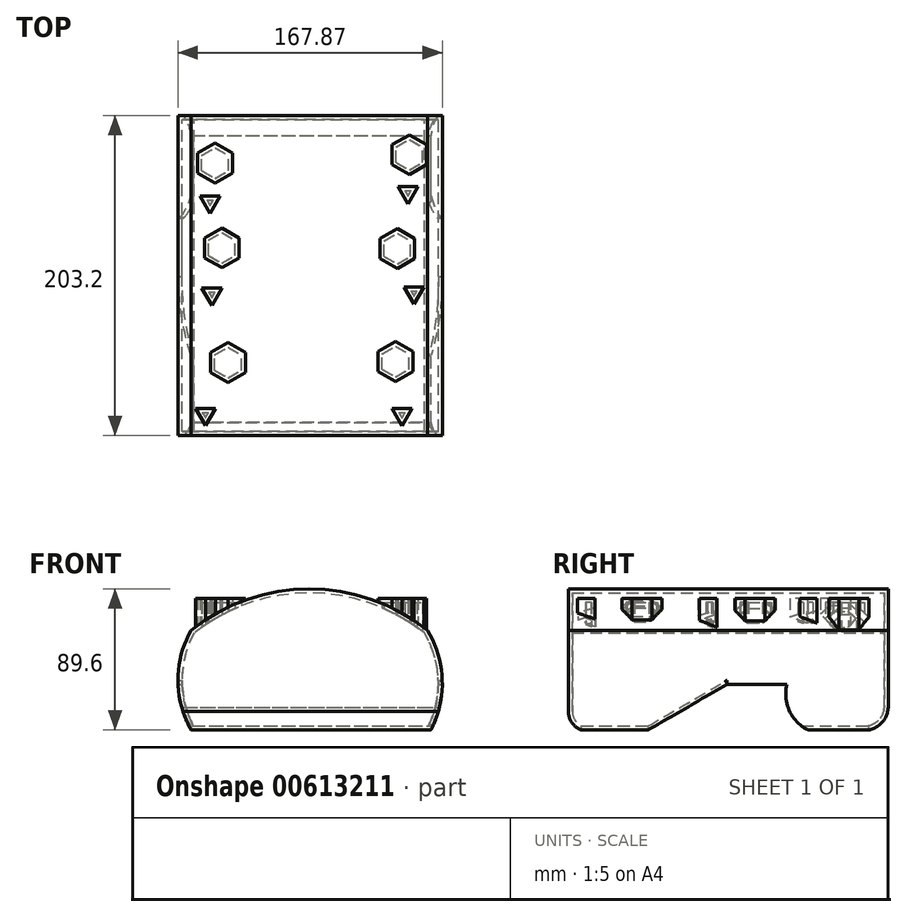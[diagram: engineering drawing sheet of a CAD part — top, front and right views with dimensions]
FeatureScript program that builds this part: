
annotation { "Feature Type Name" : "Feature", "Feature Type Description" : "" }
export const myFeature = defineFeature(function(context is Context, id is Id, definition is map)
    precondition{}
    {
        {
            var Q0;
            Q0=qCreatedBy(makeId("Front.planeOp"),FACE);
            var sketch = newSketch(context, id + "F0", { "sketchPlane" : qUnion([Q0])});
            skLineSegment(sketch, "E0", {"start": v(-76.06, 0) * mm, "end": v(76.35, 0) * mm});
            skArc(sketch, "E1", {"start": v(-76.06, 63.32) * mm, "mid": v(-84.33, 31.66) * mm, "end": v(-76.06, 0) * mm});
            skArc(sketch, "E2", {"start": v(76.35, 0) * mm, "mid": v(83.5, 31.95) * mm, "end": v(74.11, 63.32) * mm});
            skArc(sketch, "E3", {"start": v(74.11, 63.32) * mm, "mid": v(-0.97, 89.6) * mm, "end": v(-76.06, 63.32) * mm});
            skSolve(sketch);
        }
        {
            var Q0;
            Q0 = qSketchRegion(id + "F0", true);
            extrude(context, id + "F1", {"entities" : qUnion([Q0]), "depth" : 203.2 * mm, "offsetDistance" : 25.4 * mm});
        }
        {
            var Q0;
            Q0=qCreatedBy(makeId("Right.planeOp"),FACE);
            var sketch = newSketch(context, id + "F2", { "sketchPlane" : qUnion([Q0])});
            skLineSegment(sketch, "E4", {"start": v(-152.44, 0) * mm, "end": v(-102.37, 29.07) * mm});
            skArc(sketch, "E5", {"start": v(-64.27, 29.07) * mm, "mid": v(-62.7, 12.14) * mm, "end": v(-50.8, 0) * mm});
            skLineSegment(sketch, "E6", {"start": v(-102.37, 29.07) * mm, "end": v(-64.27, 29.07) * mm});
            skLineSegment(sketch, "E7", {"start": v(-152.44, 0) * mm, "end": v(-50.8, 0) * mm});
            skLineSegment(sketch, "E8.0", {"start": v(-203.2, 0) * mm, "end": v(-203.2, 63.32) * mm});
            skLineSegment(sketch, "E9.0", {"start": v(-203.2, 0) * mm, "end": v(0, 0) * mm});
            skArc(sketch, "E10", {"start": v(-203.2, 11.78) * mm, "mid": v(-200.91, 4.68) * mm, "end": v(-195.1, 0) * mm});
            skLineSegment(sketch, "E11", {"start": v(-203.2, 11.78) * mm, "end": v(-203.2, 0) * mm});
            skLineSegment(sketch, "E12", {"start": v(-195.1, 0) * mm, "end": v(-203.2, 0) * mm});
            skArc(sketch, "E13", {"start": v(-12.65, 0) * mm, "mid": v(-3.78, 4.94) * mm, "end": v(0, 14.37) * mm});
            skLineSegment(sketch, "E14", {"start": v(-12.65, 0) * mm, "end": v(0, 0) * mm});
            skLineSegment(sketch, "E15", {"start": v(0, 14.37) * mm, "end": v(0, 0) * mm});
            skSolve(sketch);
        }
        {
            var Q0;
            Q0 = qSketchRegion(id + "F2", true);
            var Q1;
            Q1=sQuery(id+"F2.wireOp",EDGE,"E4");
            var Q2;
            Q2=sQuery(id+"F2.wireOp",EDGE,"wQtt1t4y-miuZ-OvXZ-mnIg-CTxD3PF6We9W");
            var Q3;
            Q3=sQuery(id+"F2.wireOp",EDGE,"E5");
            extrude(context, id + "F3", {"entities" : qUnion([Q0]), "operationType" : NewBodyOperationType.REMOVE, "surfaceEntities" : qUnion([Q1, Q2, Q3]), "oppositeDirection" : true, "depth" : 203.2 * mm, "offsetDistance" : 25.4 * mm, "symmetric" : true});
        }
        {
            var Q0;
            Q0=makeQuery(id+"F3.boolean.opBoolean","COPY",FACE,{"derivedFrom":makeQuery(id+"F3.opExtrude","SWEPT_FACE",FACE,{"disambiguationData":[OSD([sQuery(id+"F2.wireOp",EDGE,"E6")])]})});
            var sketch = newSketch(context, id + "F4", { "sketchPlane" : qUnion([Q0])});
            skLineSegment(sketch, "E16", {"start": v(-67.5, 90.4) * mm, "end": v(-56.47, 96.7) * mm});
            skLineSegment(sketch, "E17", {"start": v(-56.47, 96.7) * mm, "end": v(-45.44, 90.4) * mm});
            skLineSegment(sketch, "E18", {"start": v(-45.44, 90.4) * mm, "end": v(-45.44, 77.7) * mm});
            skLineSegment(sketch, "E19", {"start": v(-67.5, 90.4) * mm, "end": v(-67.5, 77.7) * mm});
            skLineSegment(sketch, "E20", {"start": v(-67.5, 77.7) * mm, "end": v(-56.47, 71.4) * mm});
            skLineSegment(sketch, "E21", {"start": v(-56.47, 71.4) * mm, "end": v(-45.44, 77.7) * mm});
            skLineSegment(sketch, "E22", {"start": v(-63.65, 163.33) * mm, "end": v(-52.62, 169.63) * mm});
            skLineSegment(sketch, "E23", {"start": v(-52.62, 169.63) * mm, "end": v(-41.6, 163.33) * mm});
            skLineSegment(sketch, "E24", {"start": v(-41.6, 163.33) * mm, "end": v(-41.6, 150.63) * mm});
            skLineSegment(sketch, "E25", {"start": v(-63.65, 163.33) * mm, "end": v(-63.65, 150.63) * mm});
            skLineSegment(sketch, "E26", {"start": v(-63.65, 150.63) * mm, "end": v(-52.62, 144.34) * mm});
            skLineSegment(sketch, "E27", {"start": v(-52.62, 144.34) * mm, "end": v(-41.6, 150.63) * mm});
            skLineSegment(sketch, "E28", {"start": v(-71.84, 36.59) * mm, "end": v(-60.8, 42.89) * mm});
            skLineSegment(sketch, "E29", {"start": v(-60.8, 42.89) * mm, "end": v(-49.78, 36.59) * mm});
            skLineSegment(sketch, "E30", {"start": v(-49.78, 36.59) * mm, "end": v(-49.78, 23.89) * mm});
            skLineSegment(sketch, "E31", {"start": v(-71.84, 36.59) * mm, "end": v(-71.84, 23.89) * mm});
            skLineSegment(sketch, "E32", {"start": v(-71.84, 23.89) * mm, "end": v(-60.8, 17.59) * mm});
            skLineSegment(sketch, "E33", {"start": v(-60.8, 17.59) * mm, "end": v(-49.78, 23.89) * mm});
            skLineSegment(sketch, "E34", {"start": v(51.56, 31.3) * mm, "end": v(62.6, 37.6) * mm});
            skLineSegment(sketch, "E35", {"start": v(62.6, 37.6) * mm, "end": v(73.62, 31.3) * mm});
            skLineSegment(sketch, "E36", {"start": v(73.62, 31.3) * mm, "end": v(73.62, 18.6) * mm});
            skLineSegment(sketch, "E37", {"start": v(51.56, 31.3) * mm, "end": v(51.56, 18.6) * mm});
            skLineSegment(sketch, "E38", {"start": v(51.56, 18.6) * mm, "end": v(62.6, 12.3) * mm});
            skLineSegment(sketch, "E39", {"start": v(62.6, 12.3) * mm, "end": v(73.62, 18.6) * mm});
            skLineSegment(sketch, "E40", {"start": v(42.78, 162.7) * mm, "end": v(53.8, 169) * mm});
            skLineSegment(sketch, "E41", {"start": v(53.8, 169) * mm, "end": v(64.83, 162.7) * mm});
            skLineSegment(sketch, "E42", {"start": v(64.83, 162.7) * mm, "end": v(64.83, 150) * mm});
            skLineSegment(sketch, "E43", {"start": v(42.78, 162.7) * mm, "end": v(42.78, 150) * mm});
            skLineSegment(sketch, "E44", {"start": v(42.78, 150) * mm, "end": v(53.8, 143.7) * mm});
            skLineSegment(sketch, "E45", {"start": v(53.8, 143.7) * mm, "end": v(64.83, 150) * mm});
            skLineSegment(sketch, "E46", {"start": v(43.95, 90.94) * mm, "end": v(54.98, 97.24) * mm});
            skLineSegment(sketch, "E47", {"start": v(54.98, 97.24) * mm, "end": v(66, 90.94) * mm});
            skLineSegment(sketch, "E48", {"start": v(66, 90.94) * mm, "end": v(66, 78.24) * mm});
            skLineSegment(sketch, "E49", {"start": v(43.95, 90.94) * mm, "end": v(43.95, 78.24) * mm});
            skLineSegment(sketch, "E50", {"start": v(43.95, 78.24) * mm, "end": v(54.98, 71.94) * mm});
            skLineSegment(sketch, "E51", {"start": v(54.98, 71.94) * mm, "end": v(66, 78.24) * mm});
            skLineSegment(sketch, "E52", {"start": v(51.56, 186.24) * mm, "end": v(64.26, 186.24) * mm});
            skLineSegment(sketch, "E53", {"start": v(51.56, 186.24) * mm, "end": v(57.91, 197.24) * mm});
            skLineSegment(sketch, "E54", {"start": v(57.91, 197.24) * mm, "end": v(64.26, 186.24) * mm});
            skLineSegment(sketch, "E55", {"start": v(-73.3, 185.97) * mm, "end": v(-60.6, 185.97) * mm});
            skLineSegment(sketch, "E56", {"start": v(-73.3, 185.97) * mm, "end": v(-66.96, 196.97) * mm});
            skLineSegment(sketch, "E57", {"start": v(-66.96, 196.97) * mm, "end": v(-60.6, 185.97) * mm});
            skLineSegment(sketch, "E58", {"start": v(59.15, 108.8) * mm, "end": v(71.85, 108.8) * mm});
            skLineSegment(sketch, "E59", {"start": v(59.15, 108.8) * mm, "end": v(65.5, 119.8) * mm});
            skLineSegment(sketch, "E60", {"start": v(65.5, 119.8) * mm, "end": v(71.85, 108.8) * mm});
            skLineSegment(sketch, "E61", {"start": v(55.34, 45.22) * mm, "end": v(68.04, 45.22) * mm});
            skLineSegment(sketch, "E62", {"start": v(55.34, 45.22) * mm, "end": v(61.7, 56.22) * mm});
            skLineSegment(sketch, "E63", {"start": v(61.7, 56.22) * mm, "end": v(68.04, 45.22) * mm});
            skLineSegment(sketch, "E64", {"start": v(-70.25, 51.28) * mm, "end": v(-57.55, 51.28) * mm});
            skLineSegment(sketch, "E65", {"start": v(-70.25, 51.28) * mm, "end": v(-63.9, 62.28) * mm});
            skLineSegment(sketch, "E66", {"start": v(-63.9, 62.28) * mm, "end": v(-57.55, 51.28) * mm});
            skLineSegment(sketch, "E67", {"start": v(-69.2, 109.7) * mm, "end": v(-56.5, 109.7) * mm});
            skLineSegment(sketch, "E68", {"start": v(-69.2, 109.7) * mm, "end": v(-62.85, 120.7) * mm});
            skLineSegment(sketch, "E69", {"start": v(-62.85, 120.7) * mm, "end": v(-56.5, 109.7) * mm});
            skSolve(sketch);
        }
        {
            var Q0;
            Q0 = qSketchRegion(id + "F4", true);
            extrude(context, id + "F5", {"entities" : qUnion([Q0]), "operationType" : NewBodyOperationType.ADD, "oppositeDirection" : true, "depth" : 54.6 * mm, "offsetDistance" : 25.4 * mm});
        }
        {
            var Q0;
            Q0=makeQuery(id+"F3.boolean.opBoolean","COPY",FACE,{"derivedFrom":makeQuery(id+"F3.opExtrude","SWEPT_FACE",FACE,{"disambiguationData":[OSD([sQuery(id+"F2.wireOp",EDGE,"E4")])]})});
            var Q1;
            Q1=makeQuery(id+"F3.boolean.opBoolean","COPY",FACE,{"derivedFrom":makeQuery(id+"F3.opExtrude","SWEPT_FACE",FACE,{"disambiguationData":[OSD([sQuery(id+"F2.wireOp",EDGE,"E6")])]})});
            var Q2;
            Q2=makeQuery(id+"F3.boolean.opBoolean","COPY",FACE,{"derivedFrom":makeQuery(id+"F3.opExtrude","SWEPT_FACE",FACE,{"disambiguationData":[OSD([sQuery(id+"F2.wireOp",EDGE,"E5")])]})});
            shell(context, id + "F6", {"entities" : qUnion([Q0, Q1, Q2]), "thickness" : 2.54 * mm});
        }
        {
            var Q0;
            Q0=makeQuery(id+"F3.boolean.opBoolean","SPLIT",FACE,{"disambiguationData":[TD([makeQuery(id+"F3.opExtrude","SWEPT_FACE",FACE,{"disambiguationData":[OSD([sQuery(id+"F2.wireOp",EDGE,"E4")])]})])],"derivedFrom":makeQuery(id+"F1.opExtrude","SWEPT_FACE",FACE,{"disambiguationData":[OSD([sQuery(id+"F0.wireOp",EDGE,"E0")])]})});
            var Q1;
            Q1=makeQuery(id+"F3.boolean.opBoolean","SPLIT",FACE,{"disambiguationData":[TD([makeQuery(id+"F3.opExtrude","SWEPT_FACE",FACE,{"disambiguationData":[OSD([sQuery(id+"F2.wireOp",EDGE,"E5")])]})])],"derivedFrom":makeQuery(id+"F1.opExtrude","SWEPT_FACE",FACE,{"disambiguationData":[OSD([sQuery(id+"F0.wireOp",EDGE,"E0")])]})});
            var Q2;
            Q2=makeQuery(id+"F3.boolean.opBoolean","COPY",FACE,{"derivedFrom":makeQuery(id+"F3.opExtrude","SWEPT_FACE",FACE,{"disambiguationData":[OSD([sQuery(id+"F2.wireOp",EDGE,"E4")])]})});
            extrude(context, id + "F7", {"entities" : qUnion([Q0, Q1, Q2]), "operationType" : NewBodyOperationType.REMOVE, "oppositeDirection" : true, "depth" : 2.54 * mm, "offsetDistance" : 25.4 * mm});
        }
        {
            var Q0;
            Q0=makeQuery(id+"F7.boolean.opBoolean","COPY",FACE,{"derivedFrom":makeQuery(id+"F7.opExtrude","SWEPT_FACE",FACE,{"disambiguationData":[OSD([sQuery(id+"F2.wireOp",EDGE,"E5"),sQuery(id+"F2.wireOp",EDGE,"E9.0")])]})});
            extrude(context, id + "F8", {"entities" : qUnion([Q0]), "operationType" : NewBodyOperationType.REMOVE, "oppositeDirection" : true, "depth" : 25.4 * mm, "offsetDistance" : 25.4 * mm});
        }
    });
